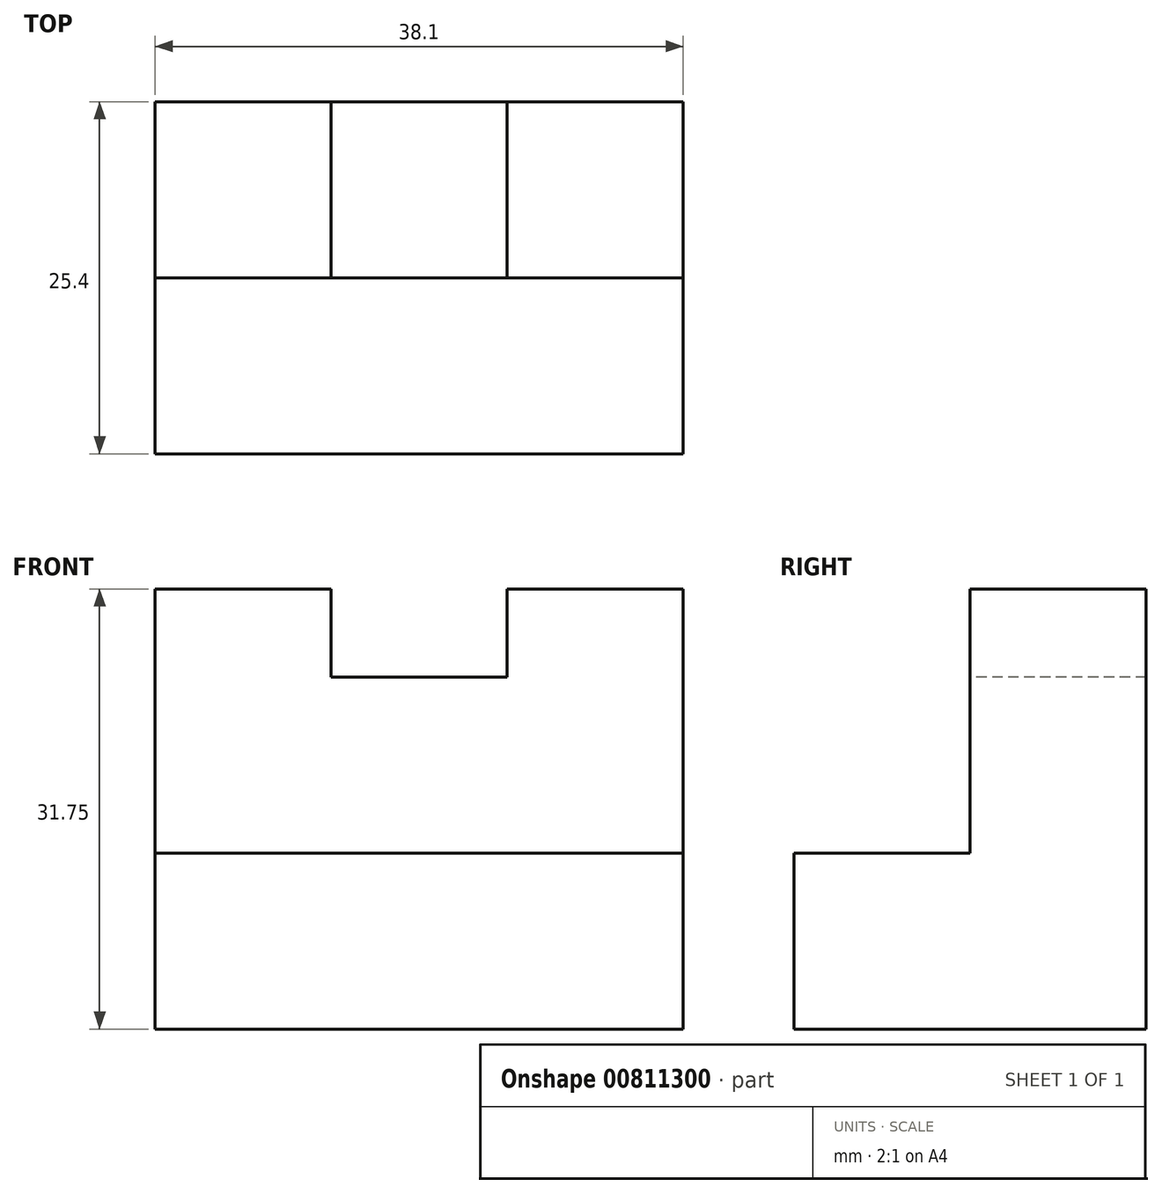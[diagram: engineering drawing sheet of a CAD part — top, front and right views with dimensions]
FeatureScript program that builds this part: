
annotation { "Feature Type Name" : "Feature", "Feature Type Description" : "" }
export const myFeature = defineFeature(function(context is Context, id is Id, definition is map)
    precondition{}
    {
        {
            var Q0;
            Q0=qCreatedBy(makeId("Right.planeOp"),FACE);
            var sketch = newSketch(context, id + "F0", { "sketchPlane" : qUnion([Q0])});
            skLineSegment(sketch, "E0", {"start": v(0, 0) * mm, "end": v(25.4, 0) * mm});
            skLineSegment(sketch, "E1", {"start": v(25.4, 0) * mm, "end": v(25.4, 31.75) * mm});
            skLineSegment(sketch, "E2", {"start": v(25.4, 31.75) * mm, "end": v(0, 31.75) * mm});
            skLineSegment(sketch, "E3", {"start": v(0, 31.75) * mm, "end": v(0, 0) * mm});
            skSolve(sketch);
        }
        {
            var Q0;
            Q0 = qSketchRegion(id + "F0", true);
            extrude(context, id + "F1", {"entities" : qUnion([Q0]), "depth" : 38.1 * mm, "offsetDistance" : 25.4 * mm});
        }
        {
            var Q0;
            Q0=makeQuery(id+"F1.opExtrude","CAP_FACE",FACE,{"disambiguationData":[OSD([sQuery(id+"F0.wireOp",EDGE,"E0"),sQuery(id+"F0.wireOp",EDGE,"E1"),sQuery(id+"F0.wireOp",EDGE,"E2"),sQuery(id+"F0.wireOp",EDGE,"E3")])],"isStart":false});
            var sketch = newSketch(context, id + "F2", { "sketchPlane" : qUnion([Q0])});
            skLineSegment(sketch, "E4", {"start": v(0, 0) * mm, "end": v(0, 12.7) * mm});
            skLineSegment(sketch, "E5", {"start": v(0, 12.7) * mm, "end": v(12.7, 12.7) * mm});
            skLineSegment(sketch, "E6", {"start": v(25.4, 31.75) * mm, "end": v(12.7, 31.75) * mm});
            skLineSegment(sketch, "E7", {"start": v(12.7, 31.75) * mm, "end": v(12.7, 12.7) * mm});
            skSolve(sketch);
        }
        {
            var Q0;
            Q0 = qSketchRegion(id + "F2", true);
            var Q1;
            {var subQ0=sQuery(id+"F2.wireOp",EDGE,"E5");Q1=makeQuery(id+"F2.imprint","IMPRINT",FACE,{"disambiguationData":[TD([[makeQuery(id+"F2.imprint","IMPRINT",EDGE,{"derivedFrom":subQ0}),1.0]])]});}
            extrude(context, id + "F3", {"entities" : qUnion([Q0, Q1]), "operationType" : NewBodyOperationType.REMOVE, "oppositeDirection" : true, "depth" : 38.1 * mm, "offsetDistance" : 25.4 * mm});
        }
        {
            var Q0;
            Q0=makeQuery(id+"F3.boolean.opBoolean","COPY",FACE,{"derivedFrom":makeQuery(id+"F3.opExtrude","SWEPT_FACE",FACE,{"disambiguationData":[OSD([sQuery(id+"F2.wireOp",EDGE,"E7")])]})});
            var sketch = newSketch(context, id + "F4", { "sketchPlane" : qUnion([Q0])});
            skLineSegment(sketch, "E8", {"start": v(0, 31.75) * mm, "end": v(12.7, 31.75) * mm});
            skLineSegment(sketch, "E9", {"start": v(12.7, 31.75) * mm, "end": v(12.7, 25.4) * mm});
            skLineSegment(sketch, "E10", {"start": v(12.7, 25.4) * mm, "end": v(25.4, 25.4) * mm});
            skLineSegment(sketch, "E11", {"start": v(25.4, 25.4) * mm, "end": v(25.4, 31.75) * mm});
            skLineSegment(sketch, "E12", {"start": v(25.4, 32.02) * mm, "end": v(38.1, 31.75) * mm});
            skSolve(sketch);
        }
        {
            var Q0;
            Q0 = qSketchRegion(id + "F4", true);
            var Q1;
            {var subQ0=sQuery(id+"F4.wireOp",EDGE,"E9");Q1=makeQuery(id+"F4.imprint","IMPRINT",FACE,{"disambiguationData":[TD([[makeQuery(id+"F4.imprint","IMPRINT",EDGE,{"derivedFrom":subQ0}),1.0]])]});}
            extrude(context, id + "F5", {"entities" : qUnion([Q0, Q1]), "operationType" : NewBodyOperationType.REMOVE, "oppositeDirection" : true, "depth" : 12.7 * mm, "offsetDistance" : 25.4 * mm});
        }
    });
